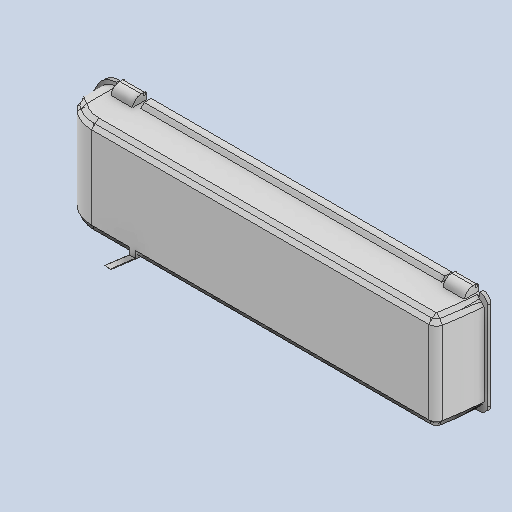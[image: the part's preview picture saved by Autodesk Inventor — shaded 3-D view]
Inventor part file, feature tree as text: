
AUTODESK INVENTOR PART (.ipt)
format: ipt  version: 2024.2 (Build 282272000, 272)  size: 223,744 bytes
history: native  units: in
note: dims shown in document units (in); Inventor stores cm internally (conversion verified against a paired STEP export)
features: chamfer x1
ambient origin geometry x8: Origin, YZ Plane, XZ Plane, XY Plane, X Axis, Y Axis, Z Axis, Center Point
bodies: Solid1 (feature_tree)
feature tree (1):
  chamfer  "Chamfer1"  [1 undecoded]
note: 1 required parameter value undecoded (feature->parameter linkage not recoverable at this tier; creation-order binding heuristic only, values carry confidence <= 0.55)
